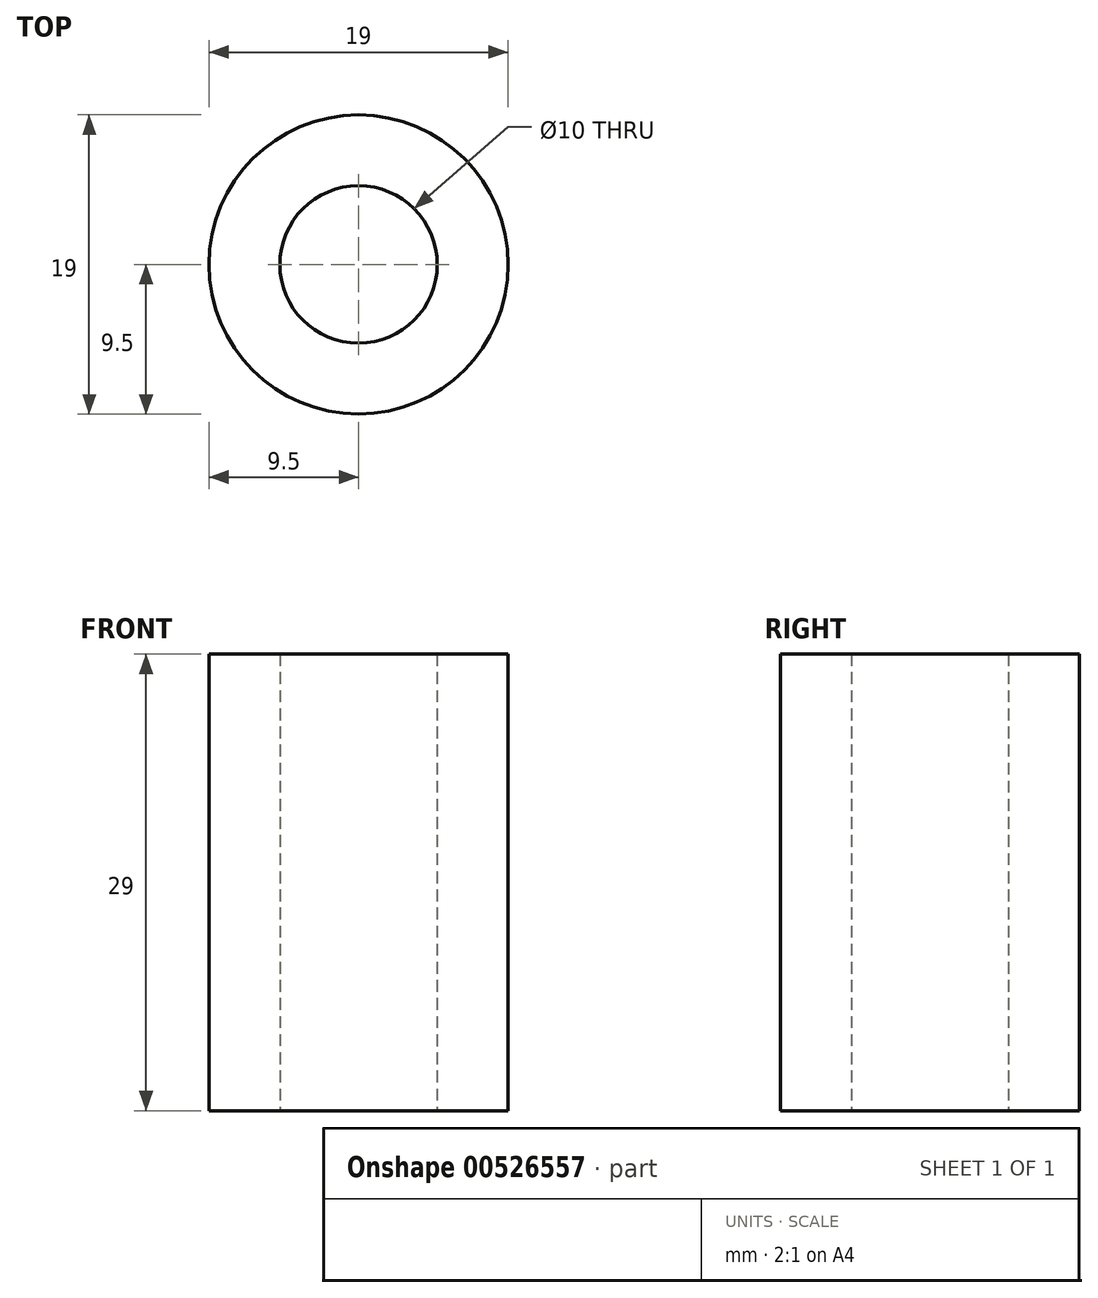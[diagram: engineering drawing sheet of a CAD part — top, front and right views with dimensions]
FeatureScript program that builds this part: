
annotation { "Feature Type Name" : "Feature", "Feature Type Description" : "" }
export const myFeature = defineFeature(function(context is Context, id is Id, definition is map)
    precondition{}
    {
        {
            var Q0;
            Q0=qCreatedBy(makeId("Top.planeOp"),FACE);
            var sketch = newSketch(context, id + "F0", { "sketchPlane" : qUnion([Q0])});
            skCircle(sketch, "E0", {"center": v(0, 0) * mm, "radius": 9.5 * mm});
            skCircle(sketch, "E1", {"center": v(0, 0) * mm, "radius": 5 * mm});
            skSolve(sketch);
        }
        {
            var Q0;
            Q0=qSketchRegion(id+"F0",true);
            extrude(context, id + "F1", {"entities" : qUnion([Q0]), "depth" : 29 * mm, "offsetDistance" : 25 * mm});
        }
    });
